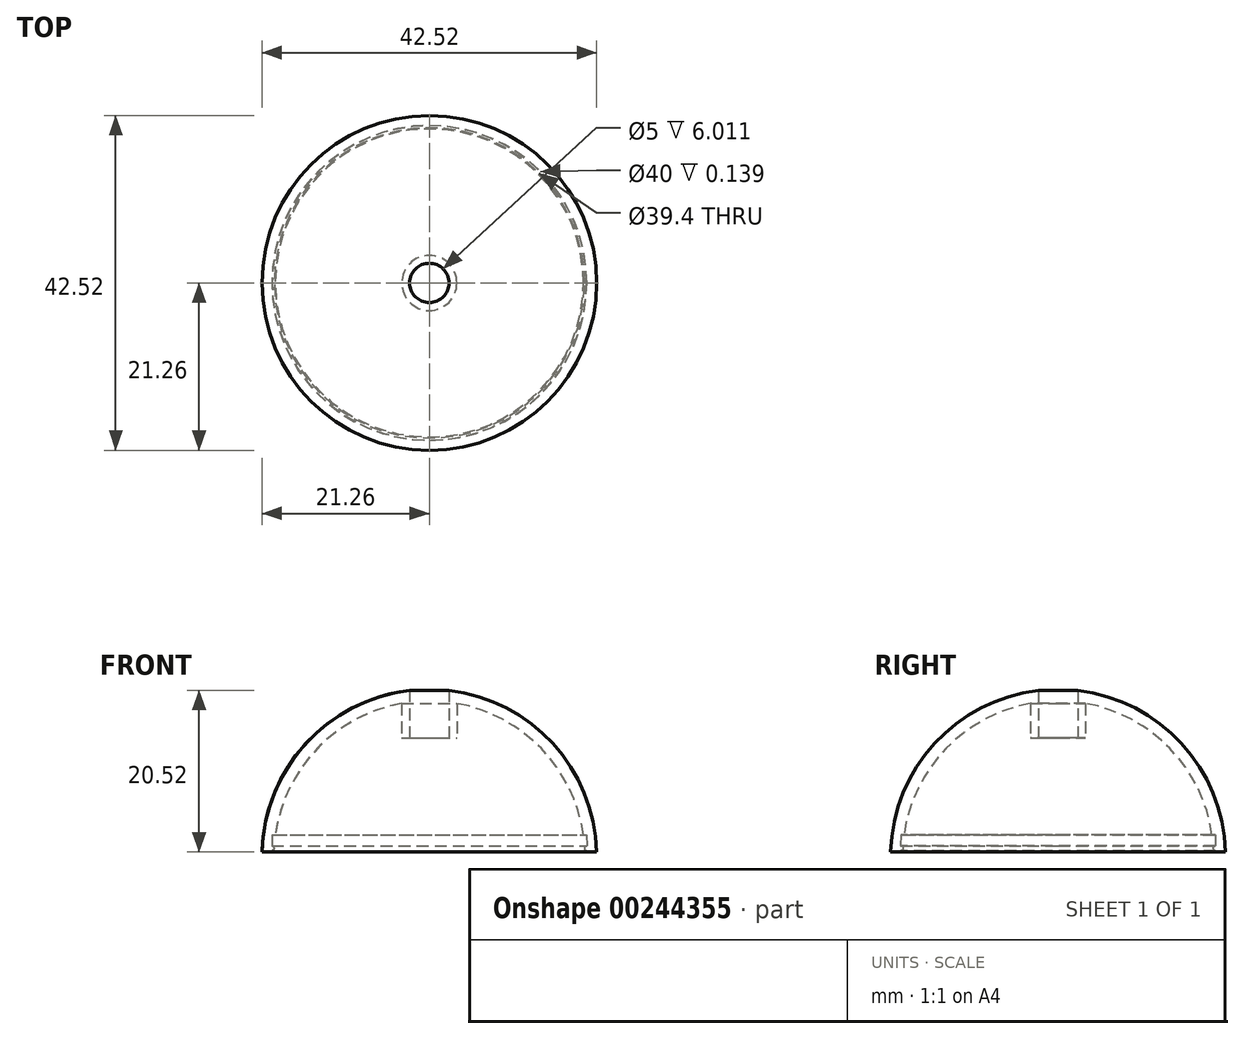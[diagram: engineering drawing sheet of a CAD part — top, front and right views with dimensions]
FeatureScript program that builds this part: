
annotation { "Feature Type Name" : "Feature", "Feature Type Description" : "" }
export const myFeature = defineFeature(function(context is Context, id is Id, definition is map)
    precondition{}
    {
        {
            var Q0;
            Q0=qCreatedBy(makeId("Front.planeOp"),FACE);
            var sketch = newSketch(context, id + "F0", { "sketchPlane" : qUnion([Q0])});
            skLineSegment(sketch, "E0", {"start": v(-21, 1.34) * mm, "end": v(-21, -1.42) * mm});
            skLineSegment(sketch, "E1", {"start": v(-21, -1.42) * mm, "end": v(-10.3, -1.42) * mm});
            skLineSegment(sketch, "E2", {"start": v(-1.7, 5.04) * mm, "end": v(-1.7, 21.8) * mm, "construction": true});
            skLineSegment(sketch, "E3", {"start": v(-2.5, 21.5) * mm, "end": v(-2.5, 14.78) * mm});
            skPoint(sketch, "E4", {"position": v(-1.7, 13.42) * mm});
            skLineSegment(sketch, "E5.bottom", {"start": v(-19.79, -0.74) * mm, "end": v(-20, -0.65) * mm});
            skLineSegment(sketch, "E5.top", {"start": v(-19.38, 0.75) * mm, "end": v(-19.97, 0.75) * mm});
            skLineSegment(sketch, "E5.right", {"start": v(-20, -0.65) * mm, "end": v(-19.97, 0.75) * mm});
            skLineSegment(sketch, "E6.trimOffspring", {"start": v(-19.7, -0.88) * mm, "end": v(-19.7, -1.03) * mm});
            skLineSegment(sketch, "E7", {"start": v(0, -11.48) * mm, "end": v(0, 19.9) * mm, "construction": true});
            skLineSegment(sketch, "E8", {"start": v(-20, -1.42) * mm, "end": v(-20, -1.28) * mm});
            skLineSegment(sketch, "E9", {"start": v(-20, -1.28) * mm, "end": v(-19.78, -1.16) * mm});
            skLineSegment(sketch, "E10.bottom", {"start": v(-2.5, 17.6) * mm, "end": v(-3.5, 17.6) * mm});
            skLineSegment(sketch, "E10.top", {"start": v(-2.5, 13.1) * mm, "end": v(-3.5, 13.1) * mm});
            skLineSegment(sketch, "E10.left", {"start": v(-2.5, 17.6) * mm, "end": v(-2.5, 13.1) * mm});
            skLineSegment(sketch, "E10.right", {"start": v(-3.5, 17.6) * mm, "end": v(-3.5, 13.1) * mm});
            skArc(sketch, "E11", {"start": v(-2.5, 19.1) * mm, "mid": v(2.1, -23.18) * mm, "end": v(-1.7, 19.18) * mm});
            skArc(sketch, "E12.0", {"start": v(-19.73, -0.77) * mm, "mid": v(14.14, -15.83) * mm, "end": v(-1.7, 17.68) * mm, "construction": true});
            skArc(sketch, "E13.trimOffspring", {"start": v(-2.5, 17.6) * mm, "mid": v(-13.88, 12.06) * mm, "end": v(-19.57, 0.75) * mm});
            skLineSegment(sketch, "E14", {"start": v(-21.17, 0) * mm, "end": v(-21, 0) * mm});
            skLineSegment(sketch, "E15", {"start": v(-21.26, -1.42) * mm, "end": v(-21, -1.42) * mm});
            skPoint(sketch, "E16.visualSharp", {"position": v(-19.7, -0.78) * mm});
            skArc(sketch, "E16.filletArc", {"start": v(-19.7, -0.88) * mm, "mid": v(-19.72, -0.8) * mm, "end": v(-19.79, -0.74) * mm});
            skPoint(sketch, "E17.visualSharp", {"position": v(-19.7, -1.12) * mm});
            skArc(sketch, "E17.filletArc", {"start": v(-19.78, -1.16) * mm, "mid": v(-19.72, -1.1) * mm, "end": v(-19.7, -1.03) * mm});
            skSolve(sketch);
        }
        {
            var Q0;
            Q0 = qSketchRegion(id + "F0", true);
            var Q1;
            Q1=sQuery(id+"F0.wireOp",EDGE,"E7");
            revolve(context, id + "F1", {"entities" : qUnion([Q0]), "axis" : qUnion([Q1]), "revolveType" : RevolveType.FULL});
        }
    });
